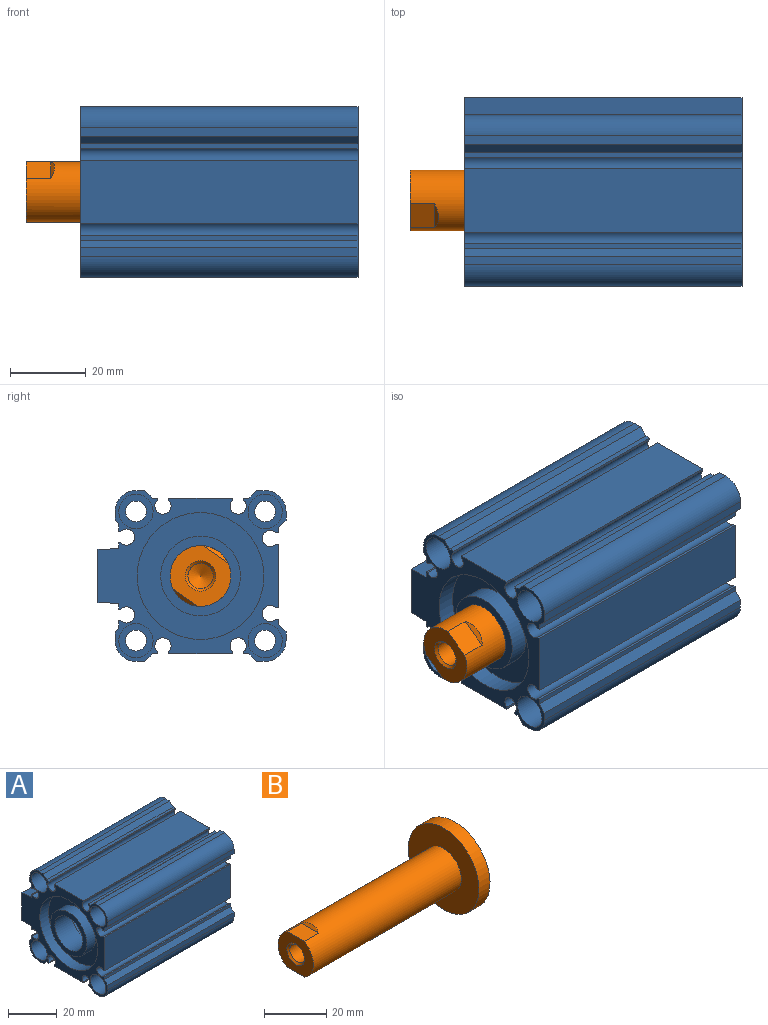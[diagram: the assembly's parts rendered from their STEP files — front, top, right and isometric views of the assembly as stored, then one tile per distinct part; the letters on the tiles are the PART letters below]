
ASSEMBLY  parts=2 mates=2
PART A: 98 faces, bbox 73x49.5x45 mm
  f0: plane 73x2.28mm, normal (0,0,1), area 166.3mm2, adj f1,f59,f60,f61
  f1: cylinder r=5.5mm len=73mm, axis (-1,0,0), area 630.7mm2, adj f0,f2,f60,f61
  f2: plane 73x2.28mm, normal (0,-1,0), area 166.3mm2, adj f1,f3,f60,f61
  f3: plane 73x2mm, normal (0,-0.71,-0.71), area 206.5mm2, adj f2,f4,f60,f61
  f4: plane 73x1.32mm, normal (0,-1,0), area 96.5mm2, adj f3,f5,f60,f61
  f5: plane 73x0.59mm, normal (0,0,-1), area 42.9mm2, adj f4,f6,f60,f61
  f6: cylinder r=2.13mm len=73mm, axis (-1,0,0), area 734mm2, adj f5,f7,f60,f61
  f7: plane 73x0.59mm, normal (0,0,1), area 42.9mm2, adj f6,f8,f60,f61
  f8: plane 73x16.8mm, normal (0,-1,0), area 1226.4mm2, adj f7,f9,f60,f61
  f9: plane 73x0.59mm, normal (0,0,-1), area 42.9mm2, adj f8,f10,f60,f61
  f10: cylinder r=2.13mm len=73mm, axis (-1,0,0), area 734mm2, adj f9,f11,f60,f61
  f11: plane 73x0.59mm, normal (0,0,1), area 42.9mm2, adj f10,f12,f60,f61
  f12: plane 73x1.32mm, normal (0,-1,0), area 96.5mm2, adj f11,f13,f60,f61
  f13: plane 73x2mm, normal (0,-0.71,0.71), area 206.5mm2, adj f12,f14,f60,f61
  f14: plane 73x2.28mm, normal (0,-1,0), area 166.3mm2, adj f13,f15,f60,f61
  f15: cylinder r=5.5mm len=73mm, axis (-1,0,0), area 630.7mm2, adj f14,f16,f60,f61
  f16: plane 73x2.28mm, normal (0,0,-1), area 166.3mm2, adj f15,f17,f60,f61
  f17: plane 73x2mm, normal (0,0.71,-0.71), area 206.5mm2, adj f16,f18,f60,f61
  f18: plane 73x1.32mm, normal (0,0,-1), area 96.5mm2, adj f17,f19,f60,f61
  f19: plane 73x0.59mm, normal (0,1,0), area 42.9mm2, adj f18,f20,f60,f61
  f20: cylinder r=2.13mm len=73mm, axis (-1,0,0), area 734mm2, adj f19,f21,f60,f61
  f21: plane 73x0.59mm, normal (0,-1,0), area 42.9mm2, adj f20,f22,f60,f61
  f22: plane 73x16.8mm, normal (0,0,-1), area 1226.4mm2, adj f21,f23,f60,f61
  f23: plane 73x0.59mm, normal (0,1,0), area 42.9mm2, adj f22,f24,f60,f61
  f24: cylinder r=2.13mm len=73mm, axis (-1,0,0), area 734mm2, adj f23,f25,f60,f61
  f25: plane 73x0.59mm, normal (0,-1,0), area 42.9mm2, adj f24,f26,f60,f61
  f26: plane 73x1.32mm, normal (0,0,-1), area 96.5mm2, adj f25,f27,f60,f61
  f27: plane 73x2mm, normal (0,-0.71,-0.71), area 206.5mm2, adj f26,f28,f60,f61
  f28: plane 73x2.28mm, normal (0,0,-1), area 166.3mm2, adj f27,f29,f60,f61
  f29: cylinder r=5.5mm len=73mm, axis (-1,0,0), area 630.7mm2, adj f28,f30,f60,f61
  f30: plane 73x2.28mm, normal (0,1,0), area 166.3mm2, adj f29,f31,f60,f61
  f31: plane 73x0.9mm, normal (0,0.71,0.71), area 92.9mm2, adj f30,f32,f60,f61
  f32: plane 73x2.07mm, normal (0,1,0), area 151.2mm2, adj f31,f33,f60,f61
  f33: plane 73x0.59mm, normal (0,0,1), area 42.9mm2, adj f32,f34,f60,f61
  f34: cylinder r=2.13mm len=73mm, axis (-1,0,0), area 734mm2, adj f33,f35,f60,f61
  f35: plane 73x0.59mm, normal (0,0,-1), area 42.9mm2, adj f34,f36,f60,f61
  f36: plane 73x1.56mm, normal (0,1,0), area 114mm2, adj f35,f37,f60,f61
  f37: plane 73x5.4mm, normal (0,0.03,-1), area 394.4mm2, adj f36,f38,f60,f61
  f38: plane 73x14mm, normal (0,1,0), area 873.3mm2, adj f37,f39,f60,f61,f72,f75
  f39: plane 73x5.4mm, normal (0,0.03,1), area 394.4mm2, adj f38,f40,f60,f61
  f40: plane 73x1.56mm, normal (0,1,0), area 114mm2, adj f39,f41,f60,f61
  f41: plane 73x0.59mm, normal (0,0,1), area 42.9mm2, adj f40,f42,f60,f61
  f42: cylinder r=2.13mm len=73mm, axis (-1,0,0), area 734mm2, adj f41,f43,f60,f61
  f43: plane 73x0.59mm, normal (0,0,-1), area 42.9mm2, adj f42,f44,f60,f61
  f44: plane 73x2.07mm, normal (0,1,0), area 151.2mm2, adj f43,f45,f60,f61
  f45: plane 73x0.9mm, normal (0,0.71,-0.71), area 92.9mm2, adj f44,f46,f60,f61
  f46: plane 73x2.28mm, normal (0,1,0), area 166.3mm2, adj f45,f47,f60,f61
  f47: cylinder r=5.5mm len=73mm, axis (-1,0,0), area 630.7mm2, adj f46,f48,f60,f61
  f48: plane 73x2.28mm, normal (0,0,1), area 166.3mm2, adj f47,f49,f60,f61
  f49: plane 73x2mm, normal (0,-0.71,0.71), area 206.5mm2, adj f48,f50,f60,f61
  f50: plane 73x1.32mm, normal (0,0,1), area 96.5mm2, adj f49,f51,f60,f61
  f51: plane 73x0.59mm, normal (0,-1,0), area 42.9mm2, adj f50,f52,f60,f61
  f52: cylinder r=2.13mm len=73mm, axis (-1,0,0), area 734mm2, adj f51,f53,f60,f61
  f53: plane 73x0.59mm, normal (0,1,0), area 42.9mm2, adj f52,f54,f60,f61
  f54: plane 73x16.8mm, normal (0,0,1), area 1226.4mm2, adj f53,f55,f60,f61
  f55: plane 73x0.59mm, normal (0,-1,0), area 42.9mm2, adj f54,f56,f60,f61
  f56: cylinder r=2.13mm len=73mm, axis (-1,0,0), area 734mm2, adj f55,f57,f60,f61
  f57: plane 73x0.59mm, normal (0,1,0), area 42.9mm2, adj f56,f58,f60,f61
  f58: plane 73x1.32mm, normal (0,0,1), area 96.5mm2, adj f57,f59,f60,f61
  f59: plane 73x2mm, normal (0,0.71,0.71), area 206.5mm2, adj f0,f58,f60,f61
  f60: plane 49.5x45mm, normal (1,0,0), area 636.8mm2, adj f0,f1,f2,f3,f4,f5,f6,f7
  f61: plane 49.5x45mm, normal (-1,0,0), area 636.8mm2, adj f0,f1,f2,f3,f4,f5,f6,f7
  f62: plane 33.4x33.4mm, normal (1,0,0), area 876.2mm2, adj f63
  f63: cylinder r=16.7mm len=33.4mm, axis (1,0,0), area 209.9mm2, adj f60,f62
  f64: cylinder r=10.5mm len=21mm, axis (-1,0,0), area 329.9mm2, adj f66,f67
  f65: cylinder r=16.7mm len=33.4mm, axis (-1,0,0), area 524.6mm2, adj f61,f66
  f66: plane 33.4x33.4mm, normal (-1,0,0), area 529.8mm2, adj f64,f65
  f67: plane 21x21mm, normal (-1,0,0), area 145.3mm2, adj f64,f68
  f68: cylinder r=8mm len=16mm, axis (1,0,0), area 502.7mm2, adj f67,f69
  f69: plane 32x32mm, normal (1,0,0), area 603.2mm2, adj f68,f70
  f70: cylinder r=16mm len=55mm, axis (1,0,0), area 5529.2mm2, adj f69,f71
  f71: plane 32x32mm, normal (-1,0,0), area 804.2mm2, adj f70
  f72: cone r=4.86mm half-angle=45deg, axis (0,1,0), area 23.6mm2, adj f38,f73
  f73: cylinder r=4.28mm len=8.57mm, axis (0,-1,0), area 151.2mm2, adj f72,f74
  f74: plane 8.57x8.57mm, normal (0,1,0), area 57.6mm2, adj f73
  f75: cone r=4.86mm half-angle=45deg, axis (0,1,0), area 23.6mm2, adj f38,f76
  f76: cylinder r=4.28mm len=8.57mm, axis (0,-1,0), area 151.2mm2, adj f75,f77
  f77: plane 8.57x8.57mm, normal (0,1,0), area 57.6mm2, adj f76
  f78: cylinder r=4.5mm len=9mm, axis (1,0,0), area 197.9mm2, adj f61,f79
  f79: plane 9x9mm, normal (-1,0,0), area 39.9mm2, adj f78,f80
  f80: cylinder r=2.75mm len=59mm, axis (1,0,0), area 1019.4mm2, adj f79,f81
  f81: plane 9x9mm, normal (1,0,0), area 39.9mm2, adj f80,f82
  f82: cylinder r=4.5mm len=9mm, axis (1,0,0), area 197.9mm2, adj f60,f81
  f83: cylinder r=4.5mm len=9mm, axis (1,0,0), area 197.9mm2, adj f61,f84
  f84: plane 9x9mm, normal (-1,0,0), area 39.9mm2, adj f83,f85
  f85: cylinder r=2.75mm len=59mm, axis (1,0,0), area 1019.4mm2, adj f84,f86
  f86: plane 9x9mm, normal (1,0,0), area 39.9mm2, adj f85,f87
  f87: cylinder r=4.5mm len=9mm, axis (1,0,0), area 197.9mm2, adj f60,f86
  f88: cylinder r=4.5mm len=9mm, axis (1,0,0), area 197.9mm2, adj f61,f89
  f89: plane 9x9mm, normal (-1,0,0), area 39.9mm2, adj f88,f90
  f90: cylinder r=2.75mm len=59mm, axis (1,0,0), area 1019.4mm2, adj f89,f91
  f91: plane 9x9mm, normal (1,0,0), area 39.9mm2, adj f90,f92
  f92: cylinder r=4.5mm len=9mm, axis (1,0,0), area 197.9mm2, adj f60,f91
  f93: cylinder r=4.5mm len=9mm, axis (1,0,0), area 197.9mm2, adj f61,f94
  f94: plane 9x9mm, normal (-1,0,0), area 39.9mm2, adj f93,f95
  f95: cylinder r=2.75mm len=59mm, axis (1,0,0), area 1019.4mm2, adj f94,f96
  f96: plane 9x9mm, normal (1,0,0), area 39.9mm2, adj f95,f97
  f97: cylinder r=4.5mm len=9mm, axis (1,0,0), area 197.9mm2, adj f60,f96
PART B: 12 faces, bbox 72x32x32 mm
  f0: plane 16x14mm, normal (-1,0,0), area 140.3mm2, adj f1,f4,f9,f11
  f1: cylinder r=8mm len=67mm, axis (1,0,0), area 3251.9mm2, adj f0,f5,f8,f9,f10,f11
  f2: cone r=0mm half-angle=60deg, axis (-1,0,0), area 40.1mm2, adj f3
  f3: cylinder r=3.32mm len=12.32mm, axis (1,0,0), area 257.3mm2, adj f2,f4
  f4: cone r=3.32mm half-angle=45deg, axis (-1,0,0), area 22mm2, adj f0,f3
  f5: plane 32x32mm, normal (-1,0,0), area 603.2mm2, adj f1,f6
  f6: cylinder r=16mm len=32mm, axis (1,0,0), area 502.7mm2, adj f5,f7
  f7: plane 32x32mm, normal (1,0,0), area 804.2mm2, adj f6
  f8: plane 7.75x1mm, normal (-0.71,0,-0.71), area 7.4mm2, adj f1,f9
  f9: plane 7.75x6.5mm, normal (0,0,-1), area 50.3mm2, adj f0,f1,f8
  f10: plane 7.75x1mm, normal (-0.71,0,0.71), area 7.4mm2, adj f1,f11
  f11: plane 7.75x6.5mm, normal (0,0,1), area 50.3mm2, adj f0,f1,f10
PLACE A at identity fixed
PLACE B rot(axis=(-1,0,0),144.9deg) t=(-7.41,0,0)mm
MATE cylindrical B.f1 <-> A.f63  axis (1,0,0) through (19.09,0,0)mm
MATE parallel B.f1 <-> A.f63  axis (1,0,0) through (57.59,0,0)mm
